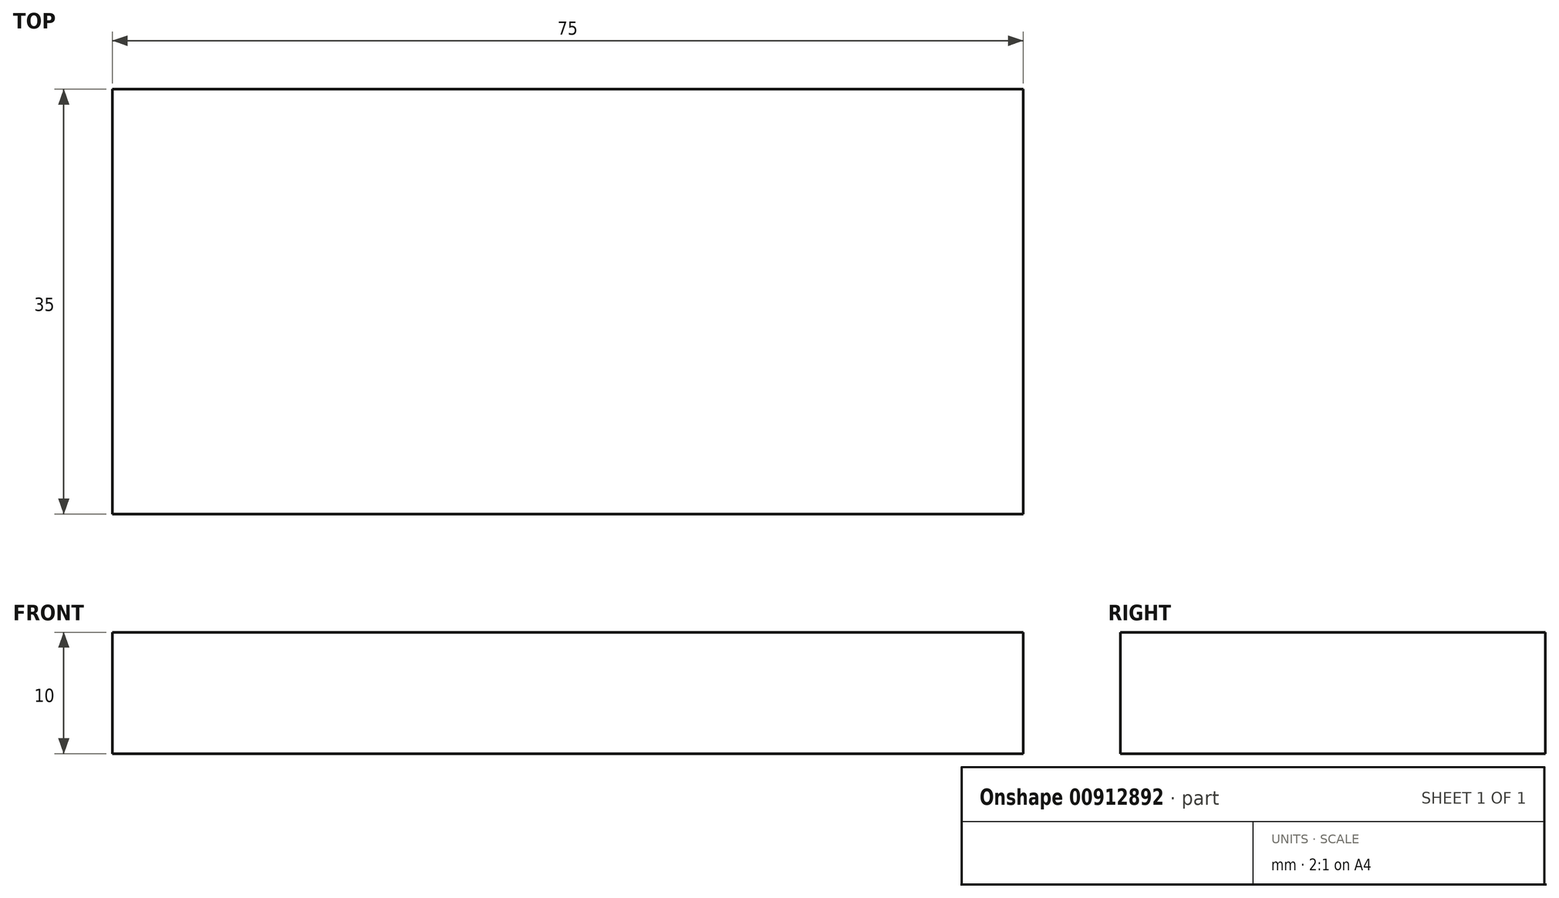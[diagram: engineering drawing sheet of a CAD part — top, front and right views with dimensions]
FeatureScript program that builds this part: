
annotation { "Feature Type Name" : "Feature", "Feature Type Description" : "" }
export const myFeature = defineFeature(function(context is Context, id is Id, definition is map)
    precondition{}
    {
        {
            var Q0;
            Q0=qCreatedBy(makeId("Top.planeOp"),FACE);
            var sketch = newSketch(context, id + "F0", { "sketchPlane" : qUnion([Q0])});
            skLineSegment(sketch, "E0.bottom", {"start": v(29.68, -54.21) * mm, "end": v(-45.32, -54.21) * mm});
            skLineSegment(sketch, "E0.top", {"start": v(29.68, -19.21) * mm, "end": v(-45.32, -19.21) * mm});
            skLineSegment(sketch, "E0.left", {"start": v(29.68, -54.21) * mm, "end": v(29.68, -19.21) * mm});
            skLineSegment(sketch, "E0.right", {"start": v(-45.32, -54.21) * mm, "end": v(-45.32, -19.21) * mm});
            skSolve(sketch);
        }
        {
            var Q0;
            Q0 = qSketchRegion(id + "F0", true);
            extrude(context, id + "F1", {"entities" : qUnion([Q0]), "depth" : 10 * mm, "offsetDistance" : 25.4 * mm});
        }
    });
